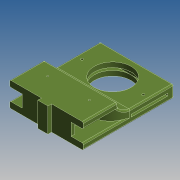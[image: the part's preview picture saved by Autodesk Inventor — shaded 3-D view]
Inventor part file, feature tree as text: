
AUTODESK INVENTOR PART (.ipt)
format: ipt  version: 2015 SP1 (Build 190203100, 203)  size: 456,704 bytes
history: native  units: mm
features: sketch x11, extrude x6, fillet x6, hole x5, projected_geometry x5, mirror x3, other x1
ambient origin geometry x8: Origin, YZ Plane, XZ Plane, XY Plane, X Axis, Y Axis, Z Axis, Center Point
bodies: Solid2 (feature_tree)
feature tree (37):
  extrude  "Extrusion2"  Depth=3.0mm
  extrude  "Extrusion3"  Depth=10.0mm TaperAngle=0.0deg
  hole  "Trou pour ressort"  [1 undecoded]
  mirror  "Mirror1"
  extrude  "Extrusion5"  Depth=3.0mm
  extrude  "Extrusion6"  Depth=2.0mm TaperAngle=0.0deg
  fillet  "Fillet3"  Radius=3.0mm
  hole  "Hole5"  [1 undecoded]
  extrude  "Extrusion13"  Depth=10.0mm TaperAngle=0.0deg
  fillet  "Fillet15"  Radius=10.0mm
  fillet  "Fillet17"  Radius=1.0mm
  fillet  "Fillet18"  Radius=1.0mm
  fillet  "Fillet19"  Radius=1.0mm
  other  "Work Axis2"
  hole  "Hole12"  [1 undecoded]
  mirror  "Mirror4"
  fillet  "Fillet25"  Radius=1.0mm
  hole  "Hole13"  [1 undecoded]
  extrude  "Extrusion18"  Depth=20.0mm
  hole  "Hole14"  [1 undecoded]
  mirror  "Mirror5"
  sketch  "Sketch1"  dims[d14=20.0mm d15=20.0mm d16=0.0mm d19=3.0mm]
  sketch  "Sketch3"  dims[d20=5.0mm d21=10.0mm d22=0.0mm]
  sketch  "Sketch6"  dims[d42=22.0mm d43=4.1mm]
  sketch  "Sketch8"  dims[d44=30.0mm d45=3.0mm]
  sketch  "Sketch9"  dims[d49=4.0mm]
  sketch  "Sketch12"  dims[d50=5.0mm d51=6.0mm d52=4.0mm d53=2.0mm d54=90.0deg d55=8.0mm d56=20.594885mm d60=2.0mm d61=0.0mm d62=3.0mm]
  sketch  "Sketch22"  dims[d66=16.0mm d67=50.0mm d68=0.0mm]
  sketch  "Sketch29"  dims[d78=11.5mm]
  projected_geometry  "Projected Loop2"
  sketch  "Sketch32"  dims[d79=6.0mm d80=6.0mm d81=4.0mm d82=2.0mm d83=90.0deg d84=8.0mm d85=20.594885mm d147=10.0mm d148=0.0mm d149=10.0mm d158=1.0mm d159=1.0mm d163=1.0mm]
  sketch  "Sketch33"  dims[d205=3.0mm]
  sketch  "Sketch34"  dims[d206=1.5mm d207=6.0mm d208=4.0mm d209=2.0mm d210=90.0deg d211=2.0mm d212=20.594885mm d213=10.0mm d214=1.0mm d223=32.0mm d224=30.0mm d225=6.0mm d226=4.0mm d227=2.0mm d228=90.0deg d229=8.0mm d230=20.594885mm d231=32.0mm d232=30.0mm d233=2.0mm d234=4.0mm d235=10.0mm d236=0.0mm d237=25.0mm d238=2.0mm d239=6.0mm d240=4.0mm d241=2.0mm d242=90.0deg d243=8.0mm d244=20.594885mm d245=20.0mm d246=17.0mm]
  projected_geometry  "Project Cut Edges2"
  projected_geometry  "Project Cut Edges4"
  projected_geometry  "Project Cut Edges5"
  projected_geometry  "Project Cut Edges7"
note: 5 required parameter values undecoded (feature->parameter linkage not recoverable at this tier; creation-order binding heuristic only, values carry confidence <= 0.55)
